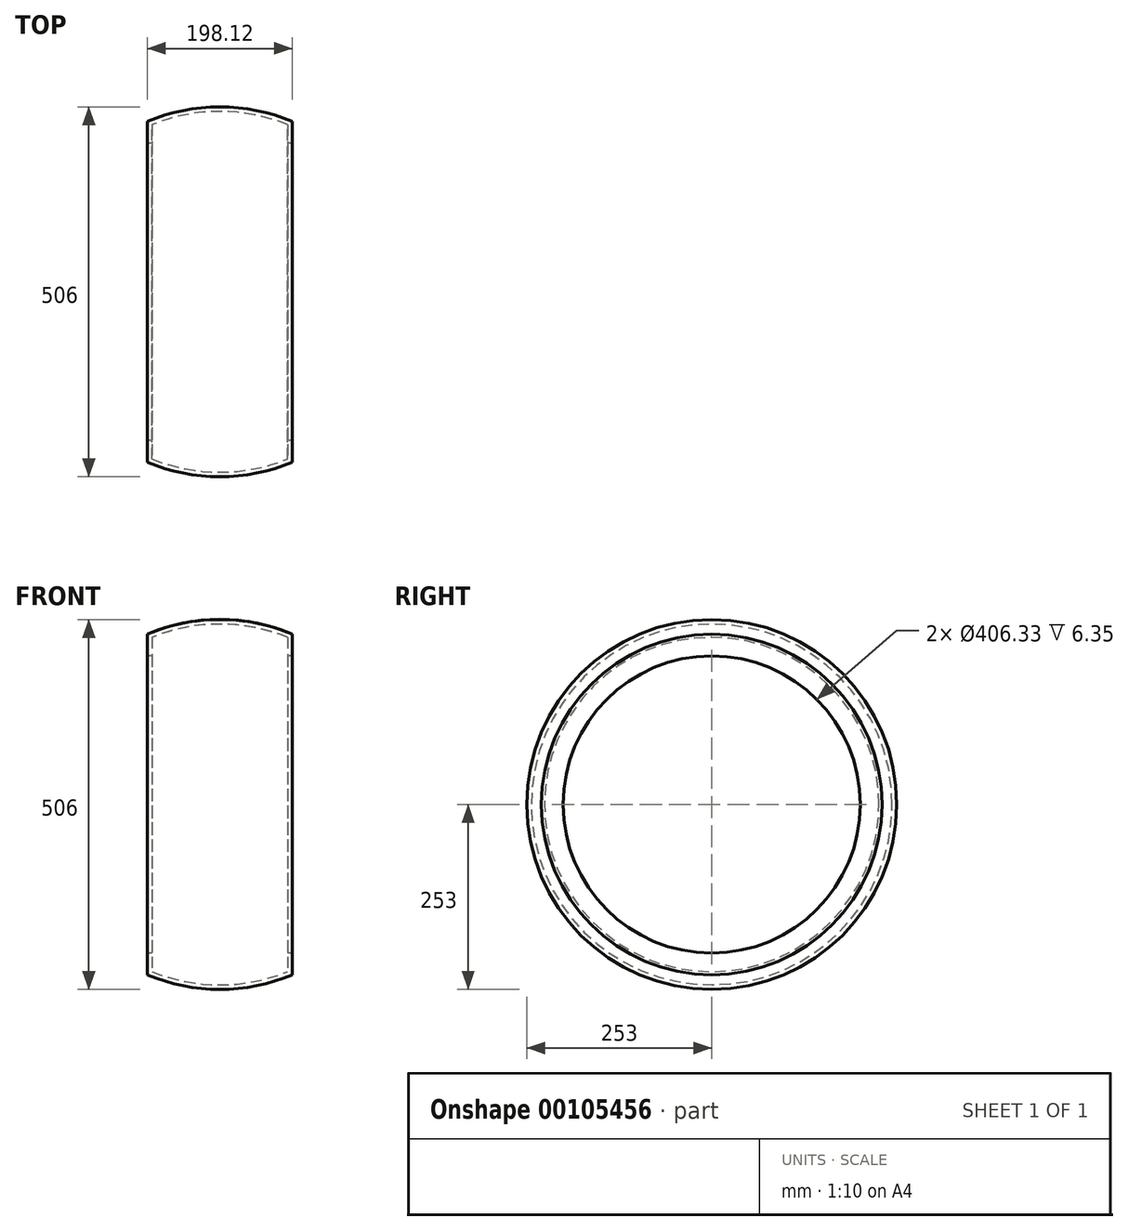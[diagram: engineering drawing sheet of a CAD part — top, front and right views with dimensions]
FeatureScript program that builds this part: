
annotation { "Feature Type Name" : "Feature", "Feature Type Description" : "" }
export const myFeature = defineFeature(function(context is Context, id is Id, definition is map)
    precondition{}
    {
        {
            var Q0;
            Q0=qCreatedBy(makeId("Top.planeOp"),FACE);
            var sketch = newSketch(context, id + "F0", { "sketchPlane" : qUnion([Q0])});
            skArc(sketch, "E0", {"start": v(-99.06, -232.8) * mm, "mid": v(0, -253) * mm, "end": v(99.06, -232.8) * mm});
            skArc(sketch, "E1.0", {"start": v(-92.71, -228.56) * mm, "mid": v(0, -246.65) * mm, "end": v(92.71, -228.56) * mm});
            skLineSegment(sketch, "E2", {"start": v(99.06, -232.8) * mm, "end": v(99.06, -203.16) * mm});
            skLineSegment(sketch, "E3.0", {"start": v(92.71, -228.56) * mm, "end": v(92.71, -203.16) * mm});
            skLineSegment(sketch, "E4", {"start": v(92.71, -203.16) * mm, "end": v(99.06, -203.16) * mm});
            skLineSegment(sketch, "E5", {"start": v(0, 0) * mm, "end": v(0, -204.73) * mm, "construction": true});
            skLineSegment(sketch, "E6.MirrorCS", {"start": v(-92.71, -228.56) * mm, "end": v(-92.71, -203.16) * mm});
            skLineSegment(sketch, "E7.MirrorCS", {"start": v(-99.06, -232.8) * mm, "end": v(-99.06, -203.16) * mm});
            skLineSegment(sketch, "E8.MirrorCS", {"start": v(-92.71, -203.16) * mm, "end": v(-99.06, -203.16) * mm});
            skLineSegment(sketch, "E9", {"start": v(0, 0) * mm, "end": v(153.5, 0) * mm, "construction": true});
            skSolve(sketch);
        }
        {
            var Q0;
            Q0 = qSketchRegion(id + "F0", true);
            var Q1;
            Q1=sQuery(id+"F0.wireOp",EDGE,"E9");
            revolve(context, id + "F1", {"entities" : qUnion([Q0]), "axis" : qUnion([Q1]), "revolveType" : RevolveType.FULL});
        }
        {
            var Q0;
            Q0=makeQuery(id+"F1.opRevolve","SWEPT_FACE",FACE,{"disambiguationData":[OSD([sQuery(id+"F0.wireOp",EDGE,"E2")])]});
            var sketch = newSketch(context, id + "F2", { "sketchPlane" : qUnion([Q0])});
            skCircle(sketch, "E10", {"center": v(-16.36, 186.94) * mm, "radius": 2 * mm});
            skCircle(sketch, "E11.1.0", {"center": v(-48.57, 181.26) * mm, "radius": 2 * mm});
            skCircle(sketch, "E11.2.0", {"center": v(-79.3, 170.07) * mm, "radius": 2 * mm});
            skCircle(sketch, "E11.3.0", {"center": v(-107.63, 153.72) * mm, "radius": 2 * mm});
            skCircle(sketch, "E11.4.0", {"center": v(-132.7, 132.7) * mm, "radius": 2 * mm});
            skCircle(sketch, "E11.5.0", {"center": v(-153.72, 107.63) * mm, "radius": 2 * mm});
            skCircle(sketch, "E11.6.0", {"center": v(-170.07, 79.3) * mm, "radius": 2 * mm});
            skCircle(sketch, "E11.7.0", {"center": v(-181.26, 48.57) * mm, "radius": 2 * mm});
            skCircle(sketch, "E11.8.0", {"center": v(-186.94, 16.36) * mm, "radius": 2 * mm});
            skCircle(sketch, "E11.9.0", {"center": v(-186.94, -16.36) * mm, "radius": 2 * mm});
            skCircle(sketch, "E11.10.0", {"center": v(-181.26, -48.57) * mm, "radius": 2 * mm});
            skCircle(sketch, "E11.11.0", {"center": v(-170.07, -79.3) * mm, "radius": 2 * mm});
            skCircle(sketch, "E11.12.0", {"center": v(-153.72, -107.63) * mm, "radius": 2 * mm});
            skCircle(sketch, "E11.13.0", {"center": v(-132.7, -132.7) * mm, "radius": 2 * mm});
            skCircle(sketch, "E11.14.0", {"center": v(-107.63, -153.72) * mm, "radius": 2 * mm});
            skCircle(sketch, "E11.15.0", {"center": v(-79.3, -170.07) * mm, "radius": 2 * mm});
            skCircle(sketch, "E11.16.0", {"center": v(-48.57, -181.26) * mm, "radius": 2 * mm});
            skCircle(sketch, "E11.17.0", {"center": v(-16.36, -186.94) * mm, "radius": 2 * mm});
            skCircle(sketch, "E11.18.0", {"center": v(16.36, -186.94) * mm, "radius": 2 * mm});
            skCircle(sketch, "E11.19.0", {"center": v(48.57, -181.26) * mm, "radius": 2 * mm});
            skCircle(sketch, "E11.20.0", {"center": v(79.3, -170.07) * mm, "radius": 2 * mm});
            skCircle(sketch, "E11.21.0", {"center": v(107.63, -153.72) * mm, "radius": 2 * mm});
            skCircle(sketch, "E11.22.0", {"center": v(132.7, -132.7) * mm, "radius": 2 * mm});
            skCircle(sketch, "E11.23.0", {"center": v(153.72, -107.63) * mm, "radius": 2 * mm});
            skCircle(sketch, "E11.24.0", {"center": v(170.07, -79.3) * mm, "radius": 2 * mm});
            skCircle(sketch, "E11.25.0", {"center": v(181.26, -48.57) * mm, "radius": 2 * mm});
            skCircle(sketch, "E11.26.0", {"center": v(186.94, -16.36) * mm, "radius": 2 * mm});
            skCircle(sketch, "E11.27.0", {"center": v(186.94, 16.36) * mm, "radius": 2 * mm});
            skCircle(sketch, "E11.28.0", {"center": v(181.26, 48.57) * mm, "radius": 2 * mm});
            skCircle(sketch, "E11.29.0", {"center": v(170.07, 79.3) * mm, "radius": 2 * mm});
            skCircle(sketch, "E11.30.0", {"center": v(153.72, 107.63) * mm, "radius": 2 * mm});
            skCircle(sketch, "E11.31.0", {"center": v(132.7, 132.7) * mm, "radius": 2 * mm});
            skCircle(sketch, "E11.32.0", {"center": v(107.63, 153.72) * mm, "radius": 2 * mm});
            skCircle(sketch, "E11.33.0", {"center": v(79.3, 170.07) * mm, "radius": 2 * mm});
            skCircle(sketch, "E11.34.0", {"center": v(48.57, 181.26) * mm, "radius": 2 * mm});
            skCircle(sketch, "E11.35.0", {"center": v(16.36, 186.94) * mm, "radius": 2 * mm});
            skPoint(sketch, "E11.center", {"position": v(0, 0) * mm});
            skSolve(sketch);
        }
        {
            var Q0;
            Q0 = qSketchRegion(id + "F2", true);
            extrude(context, id + "F3", {"entities" : qUnion([Q0]), "operationType" : NewBodyOperationType.REMOVE, "endBound" : BoundingType.THROUGH_ALL, "oppositeDirection" : true, "depth" : 25.4 * mm});
        }
    });
